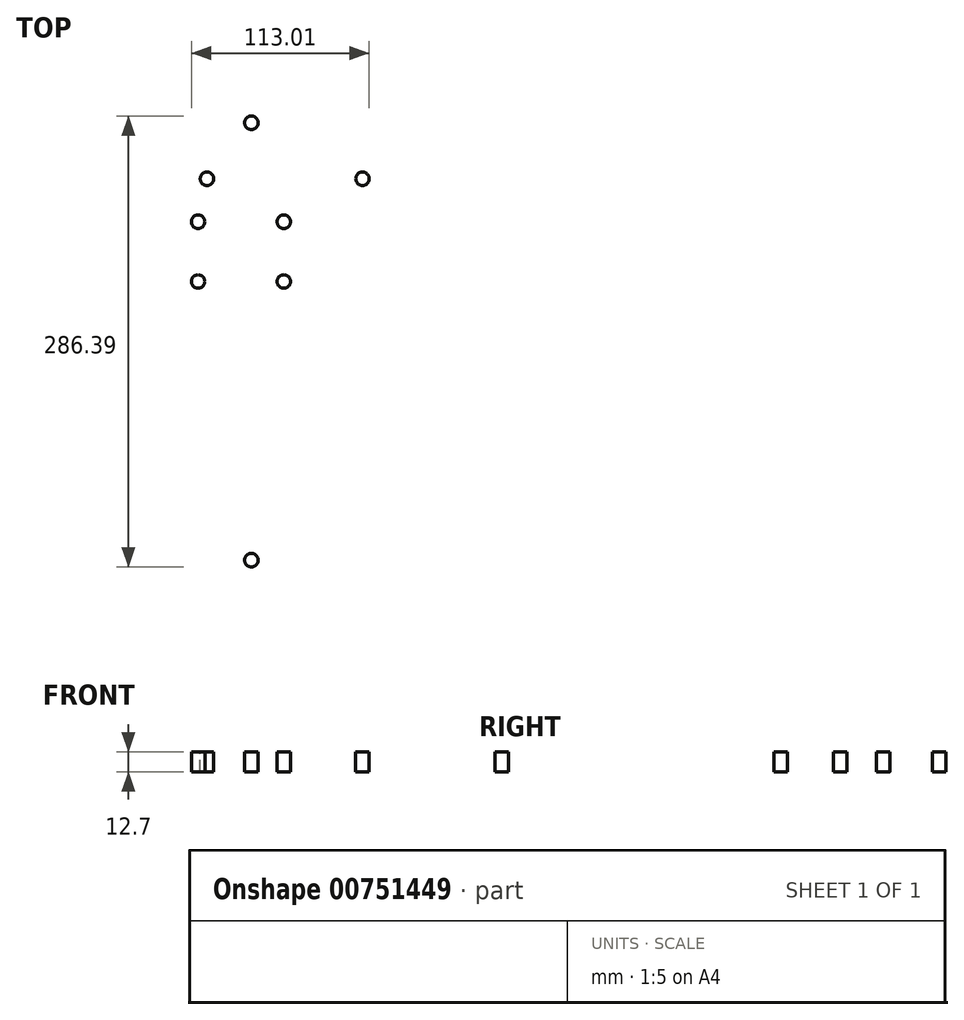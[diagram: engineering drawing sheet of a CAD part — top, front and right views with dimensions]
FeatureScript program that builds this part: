
annotation { "Feature Type Name" : "Feature", "Feature Type Description" : "" }
export const myFeature = defineFeature(function(context is Context, id is Id, definition is map)
    precondition{}
    {
        {
            var Q0;
            Q0=qCreatedBy(makeId("Top.planeOp"),FACE);
            var sketch = newSketch(context, id + "F0", { "sketchPlane" : qUnion([Q0])});
            skLineSegment(sketch, "E0.bottom", {"start": v(-266.7, 190.5) * mm, "end": v(266.7, 190.5) * mm});
            skLineSegment(sketch, "E0.top", {"start": v(-266.7, -190.5) * mm, "end": v(266.7, -190.5) * mm});
            skLineSegment(sketch, "E0.left", {"start": v(-266.7, 190.5) * mm, "end": v(-266.7, -190.5) * mm});
            skLineSegment(sketch, "E0.right", {"start": v(266.7, 190.5) * mm, "end": v(266.7, -190.5) * mm});
            skLineSegment(sketch, "E1", {"start": v(-266.7, 190.5) * mm, "end": v(266.7, -190.5) * mm, "construction": true});
            skLineSegment(sketch, "E2", {"start": v(266.7, 190.5) * mm, "end": v(-266.7, -190.5) * mm, "construction": true});
            skPoint(sketch, "E3", {"position": v(0, 0) * mm});
            skSolve(sketch);
        }
        {
            var Q0;
            Q0=makeQuery(id+"F0.imprint","IMPRINT",FACE,{"disambiguationData":[TD([[makeQuery(id+"F0.imprint","IMPRINT",EDGE,{"derivedFrom":sQuery(id+"F0.wireOp",EDGE,"E0.bottom")}),-1.0]])]});
            extrude(context, id + "F1", {"entities" : qUnion([Q0]), "depth" : 12.7 * mm, "offsetDistance" : 25.4 * mm});
        }
        {
            var Q0;
            Q0=makeQuery(id+"F1.opExtrude","CAP_FACE",FACE,{"disambiguationData":[OSD([sQuery(id+"F0.wireOp",EDGE,"E0.bottom"),sQuery(id+"F0.wireOp",EDGE,"E0.top"),sQuery(id+"F0.wireOp",EDGE,"E0.left"),sQuery(id+"F0.wireOp",EDGE,"E0.right")])],"isStart":false});
            var sketch = newSketch(context, id + "F2", { "sketchPlane" : qUnion([Q0])});
            skLineSegment(sketch, "E4.bottom", {"start": v(173.08, 152.4) * mm, "end": v(236.58, 152.4) * mm});
            skLineSegment(sketch, "E4.top", {"start": v(173.08, 63.5) * mm, "end": v(236.58, 63.5) * mm});
            skLineSegment(sketch, "E4.left", {"start": v(173.08, 152.4) * mm, "end": v(173.08, 63.5) * mm});
            skLineSegment(sketch, "E4.right", {"start": v(236.58, 152.4) * mm, "end": v(236.58, 63.5) * mm});
            skLineSegment(sketch, "E5.bottom", {"start": v(208.28, 28.07) * mm, "end": v(87.63, 28.07) * mm, "construction": true});
            skLineSegment(sketch, "E5.top", {"start": v(208.28, 92.08) * mm, "end": v(87.63, 92.07) * mm, "construction": true});
            skLineSegment(sketch, "E5.left", {"start": v(208.28, 28.07) * mm, "end": v(208.28, 92.08) * mm, "construction": true});
            skLineSegment(sketch, "E5.right", {"start": v(87.63, 28.07) * mm, "end": v(87.63, 92.07) * mm, "construction": true});
            skCircle(sketch, "E6", {"center": v(108.03, 79.06) * mm, "radius": 4.3 * mm});
            skCircle(sketch, "E7", {"center": v(108.03, 41.08) * mm, "radius": 4.3 * mm});
            skCircle(sketch, "E8", {"center": v(162.48, 41.08) * mm, "radius": 4.3 * mm});
            skCircle(sketch, "E9", {"center": v(162.48, 79.06) * mm, "radius": 4.3 * mm});
            skLineSegment(sketch, "E10.bottom", {"start": v(131, 125.41) * mm, "end": v(173.08, 125.41) * mm, "construction": true});
            skLineSegment(sketch, "E10.top", {"start": v(131, 87.31) * mm, "end": v(173.08, 87.31) * mm, "construction": true});
            skLineSegment(sketch, "E10.left", {"start": v(131, 125.41) * mm, "end": v(131, 87.31) * mm, "construction": true});
            skLineSegment(sketch, "E10.right", {"start": v(173.08, 125.41) * mm, "end": v(173.08, 87.31) * mm, "construction": true});
            skCircle(sketch, "E11", {"center": v(156.81, 106.36) * mm, "radius": 4.3 * mm});
            skPoint(sketch, "E12", {"position": v(173.08, 106.36) * mm});
            skLineSegment(sketch, "E13.bottom", {"start": v(40.4, 125.41) * mm, "end": v(101.52, 125.41) * mm, "construction": true});
            skLineSegment(sketch, "E13.top", {"start": v(40.4, 87.31) * mm, "end": v(101.52, 87.31) * mm, "construction": true});
            skLineSegment(sketch, "E13.left", {"start": v(40.4, 125.41) * mm, "end": v(40.4, 87.31) * mm, "construction": true});
            skLineSegment(sketch, "E13.right", {"start": v(101.52, 125.41) * mm, "end": v(101.52, 87.31) * mm, "construction": true});
            skCircle(sketch, "E14", {"center": v(58.04, 106.36) * mm, "radius": 4.29 * mm});
            skPoint(sketch, "E14.perimeterSnap0", {"position": v(40.4, 106.36) * mm});
            skLineSegment(sketch, "E15", {"start": v(0, 190.5) * mm, "end": v(0, -190.5) * mm, "construction": true});
            skLineSegment(sketch, "E16.MirrorCS", {"start": v(-40.4, 125.41) * mm, "end": v(-40.4, 87.31) * mm, "construction": true});
            skLineSegment(sketch, "E17.MirrorCS", {"start": v(-40.4, 87.31) * mm, "end": v(-101.52, 87.31) * mm, "construction": true});
            skLineSegment(sketch, "E18.MirrorCS", {"start": v(-101.52, 125.41) * mm, "end": v(-101.52, 87.31) * mm, "construction": true});
            skLineSegment(sketch, "E19.MirrorCS", {"start": v(-40.4, 125.41) * mm, "end": v(-101.52, 125.41) * mm, "construction": true});
            skCircle(sketch, "E20.MirrorC", {"center": v(-58.04, 106.36) * mm, "radius": 4.29 * mm});
            skPoint(sketch, "E21.MirrorP", {"position": v(-40.4, 106.36) * mm});
            skLineSegment(sketch, "E22.MirrorCS", {"start": v(-87.63, 28.07) * mm, "end": v(-87.63, 92.08) * mm, "construction": true});
            skLineSegment(sketch, "E23.MirrorCS", {"start": v(-208.28, 28.07) * mm, "end": v(-87.63, 28.07) * mm, "construction": true});
            skLineSegment(sketch, "E24.MirrorCS", {"start": v(-208.28, 92.08) * mm, "end": v(-87.63, 92.08) * mm, "construction": true});
            skLineSegment(sketch, "E25.MirrorCS", {"start": v(-131, 125.41) * mm, "end": v(-131, 87.31) * mm, "construction": true});
            skLineSegment(sketch, "E26.MirrorCS", {"start": v(-208.28, 28.07) * mm, "end": v(-208.28, 92.08) * mm, "construction": true});
            skLineSegment(sketch, "E27.MirrorCS", {"start": v(-173.08, 125.41) * mm, "end": v(-173.08, 87.31) * mm, "construction": true});
            skPoint(sketch, "E28.MirrorP", {"position": v(-173.08, 106.36) * mm});
            skLineSegment(sketch, "E29.MirrorCS", {"start": v(-173.08, 152.4) * mm, "end": v(-173.08, 63.5) * mm});
            skLineSegment(sketch, "E30.MirrorCS", {"start": v(-173.08, 152.4) * mm, "end": v(-236.58, 152.4) * mm});
            skLineSegment(sketch, "E31.MirrorCS", {"start": v(-236.58, 152.4) * mm, "end": v(-236.58, 63.5) * mm});
            skLineSegment(sketch, "E32.MirrorCS", {"start": v(-173.08, 63.5) * mm, "end": v(-236.58, 63.5) * mm});
            skLineSegment(sketch, "E33.MirrorCS", {"start": v(-131, 87.31) * mm, "end": v(-173.08, 87.31) * mm, "construction": true});
            skLineSegment(sketch, "E34.MirrorCS", {"start": v(-131, 125.41) * mm, "end": v(-173.08, 125.41) * mm, "construction": true});
            skCircle(sketch, "E35.MirrorC", {"center": v(-156.81, 106.36) * mm, "radius": 4.3 * mm});
            skCircle(sketch, "E36.MirrorC", {"center": v(-108.03, 79.06) * mm, "radius": 4.3 * mm});
            skCircle(sketch, "E37.MirrorC", {"center": v(-108.03, 41.08) * mm, "radius": 4.3 * mm});
            skCircle(sketch, "E38.MirrorC", {"center": v(-162.48, 41.08) * mm, "radius": 4.3 * mm});
            skCircle(sketch, "E39.MirrorC", {"center": v(-162.48, 79.06) * mm, "radius": 4.3 * mm});
            skCircle(sketch, "E40", {"center": v(128.63, 141.92) * mm, "radius": 4.29 * mm});
            skCircle(sketch, "E41.MirrorC", {"center": v(-128.63, 141.92) * mm, "radius": 4.29 * mm});
            skCircle(sketch, "E42", {"center": v(128.63, -135.9) * mm, "radius": 4.29 * mm, "construction": true});
            skCircle(sketch, "E43.MirrorC", {"center": v(-128.63, -135.89) * mm, "radius": 4.29 * mm});
            skLineSegment(sketch, "E44.bottom", {"start": v(-12.7, 97.47) * mm, "end": v(12.7, 97.47) * mm});
            skLineSegment(sketch, "E44.top", {"start": v(-12.7, 91.12) * mm, "end": v(12.7, 91.12) * mm});
            skLineSegment(sketch, "E44.left", {"start": v(-12.7, 97.47) * mm, "end": v(-12.7, 91.12) * mm});
            skLineSegment(sketch, "E44.right", {"start": v(12.7, 97.47) * mm, "end": v(12.7, 91.12) * mm});
            skPoint(sketch, "E45", {"position": v(0, 91.12) * mm});
            skLineSegment(sketch, "E46.bottom", {"start": v(-12.7, -8.76) * mm, "end": v(12.7, -8.76) * mm});
            skLineSegment(sketch, "E46.top", {"start": v(-12.7, -15.11) * mm, "end": v(12.7, -15.11) * mm});
            skLineSegment(sketch, "E46.left", {"start": v(-12.7, -8.76) * mm, "end": v(-12.7, -15.11) * mm});
            skLineSegment(sketch, "E46.right", {"start": v(12.7, -8.76) * mm, "end": v(12.7, -15.11) * mm});
            skPoint(sketch, "E47", {"position": v(0, -8.76) * mm});
            skLineSegment(sketch, "E48.bottom", {"start": v(-84.46, 53.47) * mm, "end": v(-78.1, 53.47) * mm});
            skLineSegment(sketch, "E48.top", {"start": v(-84.46, 28.07) * mm, "end": v(-78.1, 28.07) * mm});
            skLineSegment(sketch, "E48.left", {"start": v(-84.46, 53.47) * mm, "end": v(-84.46, 28.07) * mm});
            skLineSegment(sketch, "E48.right", {"start": v(-78.1, 53.47) * mm, "end": v(-78.1, 28.07) * mm});
            skLineSegment(sketch, "E49.MirrorCS", {"start": v(78.1, 53.47) * mm, "end": v(78.1, 28.07) * mm});
            skLineSegment(sketch, "E50.MirrorCS", {"start": v(84.46, 53.47) * mm, "end": v(78.1, 53.47) * mm});
            skLineSegment(sketch, "E51.MirrorCS", {"start": v(84.46, 53.47) * mm, "end": v(84.46, 28.07) * mm});
            skLineSegment(sketch, "E52.MirrorCS", {"start": v(84.46, 28.07) * mm, "end": v(78.1, 28.07) * mm});
            skLineSegment(sketch, "E53.bottom", {"start": v(90.53, -120.02) * mm, "end": v(166.73, -120.02) * mm, "construction": true});
            skLineSegment(sketch, "E53.top", {"start": v(90.53, -151.77) * mm, "end": v(166.73, -151.77) * mm, "construction": true});
            skLineSegment(sketch, "E53.left", {"start": v(90.53, -120.02) * mm, "end": v(90.53, -151.77) * mm, "construction": true});
            skLineSegment(sketch, "E53.right", {"start": v(166.73, -120.02) * mm, "end": v(166.73, -151.77) * mm, "construction": true});
            skLineSegment(sketch, "E54", {"start": v(166.73, -120.02) * mm, "end": v(90.53, -151.77) * mm, "construction": true});
            skLineSegment(sketch, "E55", {"start": v(90.53, -120.02) * mm, "end": v(166.73, -151.77) * mm, "construction": true});
            skLineSegment(sketch, "E56.MirrorCS", {"start": v(-166.73, -120.02) * mm, "end": v(-90.53, -151.77) * mm, "construction": true});
            skLineSegment(sketch, "E57.MirrorCS", {"start": v(-90.53, -120.01) * mm, "end": v(-166.73, -151.77) * mm, "construction": true});
            skLineSegment(sketch, "E58.MirrorCS", {"start": v(-90.53, -120.02) * mm, "end": v(-166.73, -120.02) * mm, "construction": true});
            skLineSegment(sketch, "E59.MirrorCS", {"start": v(-90.53, -151.77) * mm, "end": v(-166.73, -151.77) * mm, "construction": true});
            skLineSegment(sketch, "E60.MirrorCS", {"start": v(-166.73, -120.02) * mm, "end": v(-166.73, -151.77) * mm, "construction": true});
            skCircle(sketch, "E61.MirrorC", {"center": v(-128.63, -135.89) * mm, "radius": 4.29 * mm, "construction": true});
            skLineSegment(sketch, "E62.MirrorCS", {"start": v(-90.53, -120.02) * mm, "end": v(-90.53, -151.77) * mm, "construction": true});
            skSolve(sketch);
        }
        {
            var Q0;
            Q0=makeQuery(id+"F2.imprint","IMPRINT",FACE,{"disambiguationData":[TD([[makeQuery(id+"F2.imprint","IMPRINT",EDGE,{"derivedFrom":sQuery(id+"F2.wireOp",EDGE,"E4.bottom")}),-1.0]])]});
            var Q1;
            Q1=makeQuery(id+"F2.imprint","IMPRINT",FACE,{"disambiguationData":[TD([[makeQuery(id+"F2.imprint","IMPRINT",EDGE,{"derivedFrom":sQuery(id+"F2.wireOp",EDGE,"E6")}),1.0]])]});
            var Q2;
            Q2=makeQuery(id+"F2.imprint","IMPRINT",FACE,{"disambiguationData":[TD([[makeQuery(id+"F2.imprint","IMPRINT",EDGE,{"derivedFrom":sQuery(id+"F2.wireOp",EDGE,"E9")}),1.0]])]});
            var Q3;
            Q3=makeQuery(id+"F2.imprint","IMPRINT",FACE,{"disambiguationData":[TD([[makeQuery(id+"F2.imprint","IMPRINT",EDGE,{"derivedFrom":sQuery(id+"F2.wireOp",EDGE,"E8")}),1.0]])]});
            var Q4;
            Q4=makeQuery(id+"F2.imprint","IMPRINT",FACE,{"disambiguationData":[TD([[makeQuery(id+"F2.imprint","IMPRINT",EDGE,{"derivedFrom":sQuery(id+"F2.wireOp",EDGE,"E7")}),1.0]])]});
            var Q5;
            Q5=makeQuery(id+"F2.imprint","IMPRINT",FACE,{"disambiguationData":[TD([[makeQuery(id+"F2.imprint","IMPRINT",EDGE,{"derivedFrom":sQuery(id+"F2.wireOp",EDGE,"E14")}),1.0]])]});
            var Q6;
            Q6=makeQuery(id+"F2.imprint","IMPRINT",FACE,{"disambiguationData":[TD([[makeQuery(id+"F2.imprint","IMPRINT",EDGE,{"derivedFrom":sQuery(id+"F2.wireOp",EDGE,"E11")}),1.0]])]});
            var Q7;
            Q7=makeQuery(id+"F2.imprint","IMPRINT",FACE,{"disambiguationData":[TD([[makeQuery(id+"F2.imprint","IMPRINT",EDGE,{"derivedFrom":sQuery(id+"F2.wireOp",EDGE,"E29.MirrorCS")}),-1.0]])]});
            var Q8;
            Q8=makeQuery(id+"F2.imprint","IMPRINT",FACE,{"disambiguationData":[TD([[makeQuery(id+"F2.imprint","IMPRINT",EDGE,{"derivedFrom":sQuery(id+"F2.wireOp",EDGE,"E39.MirrorC")}),-1.0]])]});
            var Q9;
            Q9=makeQuery(id+"F2.imprint","IMPRINT",FACE,{"disambiguationData":[TD([[makeQuery(id+"F2.imprint","IMPRINT",EDGE,{"derivedFrom":sQuery(id+"F2.wireOp",EDGE,"E38.MirrorC")}),-1.0]])]});
            var Q10;
            Q10=makeQuery(id+"F2.imprint","IMPRINT",FACE,{"disambiguationData":[TD([[makeQuery(id+"F2.imprint","IMPRINT",EDGE,{"derivedFrom":sQuery(id+"F2.wireOp",EDGE,"E37.MirrorC")}),-1.0]])]});
            var Q11;
            Q11=makeQuery(id+"F2.imprint","IMPRINT",FACE,{"disambiguationData":[TD([[makeQuery(id+"F2.imprint","IMPRINT",EDGE,{"derivedFrom":sQuery(id+"F2.wireOp",EDGE,"E36.MirrorC")}),-1.0]])]});
            var Q12;
            Q12=makeQuery(id+"F2.imprint","IMPRINT",FACE,{"disambiguationData":[TD([[makeQuery(id+"F2.imprint","IMPRINT",EDGE,{"derivedFrom":sQuery(id+"F2.wireOp",EDGE,"E35.MirrorC")}),-1.0]])]});
            var Q13;
            Q13=makeQuery(id+"F2.imprint","IMPRINT",FACE,{"disambiguationData":[TD([[makeQuery(id+"F2.imprint","IMPRINT",EDGE,{"derivedFrom":sQuery(id+"F2.wireOp",EDGE,"E20.MirrorC")}),-1.0]])]});
            var Q14;
            Q14=makeQuery(id+"F2.imprint","IMPRINT",FACE,{"disambiguationData":[TD([[makeQuery(id+"F2.imprint","IMPRINT",EDGE,{"derivedFrom":sQuery(id+"F2.wireOp",EDGE,"E40")}),1.0]])]});
            var Q15;
            Q15=makeQuery(id+"F2.imprint","IMPRINT",FACE,{"disambiguationData":[TD([[makeQuery(id+"F2.imprint","IMPRINT",EDGE,{"derivedFrom":sQuery(id+"F2.wireOp",EDGE,"E41.MirrorC")}),-1.0]])]});
            var Q16;
            Q16=makeQuery(id+"F2.imprint","IMPRINT",FACE,{"disambiguationData":[TD([[makeQuery(id+"F2.imprint","IMPRINT",EDGE,{"derivedFrom":sQuery(id+"F2.wireOp",EDGE,"E42")}),1.0]])]});
            var Q17;
            Q17=makeQuery(id+"F2.imprint","IMPRINT",FACE,{"disambiguationData":[TD([[makeQuery(id+"F2.imprint","IMPRINT",EDGE,{"derivedFrom":sQuery(id+"F2.wireOp",EDGE,"E43.MirrorC")}),-1.0]])]});
            var Q18;
            Q18=makeQuery(id+"F2.imprint","IMPRINT",FACE,{"disambiguationData":[TD([[makeQuery(id+"F2.imprint","IMPRINT",EDGE,{"derivedFrom":sQuery(id+"F2.wireOp",EDGE,"E48.bottom")}),-1.0]])]});
            var Q19;
            Q19=makeQuery(id+"F2.imprint","IMPRINT",FACE,{"disambiguationData":[TD([[makeQuery(id+"F2.imprint","IMPRINT",EDGE,{"derivedFrom":sQuery(id+"F2.wireOp",EDGE,"E44.bottom")}),-1.0]])]});
            var Q20;
            Q20=makeQuery(id+"F2.imprint","IMPRINT",FACE,{"disambiguationData":[TD([[makeQuery(id+"F2.imprint","IMPRINT",EDGE,{"derivedFrom":sQuery(id+"F2.wireOp",EDGE,"E49.MirrorCS")}),1.0]])]});
            var Q21;
            Q21=makeQuery(id+"F2.imprint","IMPRINT",FACE,{"disambiguationData":[TD([[makeQuery(id+"F2.imprint","IMPRINT",EDGE,{"derivedFrom":sQuery(id+"F2.wireOp",EDGE,"E46.bottom")}),-1.0]])]});
            extrude(context, id + "F3", {"entities" : qUnion([Q0, Q1, Q2, Q3, Q4, Q5, Q6, Q7, Q8, Q9, Q10, Q11, Q12, Q13, Q14, Q15, Q16, Q17, Q18, Q19, Q20, Q21]), "operationType" : NewBodyOperationType.REMOVE, "endBound" : BoundingType.THROUGH_ALL, "oppositeDirection" : true, "depth" : 25.4 * mm, "offsetDistance" : 25.4 * mm});
        }
        {
            var Q0;
            Q0=makeQuery(id+"F2.imprint","IMPRINT",FACE,{"disambiguationData":[TD([[makeQuery(id+"F2.imprint","IMPRINT",EDGE,{"derivedFrom":sQuery(id+"F2.wireOp",EDGE,"E4.bottom")}),1.0]])]});
            var sketch = newSketch(context, id + "F4", { "sketchPlane" : qUnion([Q0])});
            skLineSegment(sketch, "E63.bottom", {"start": v(-75, 87.31) * mm, "end": v(75, 87.31) * mm});
            skLineSegment(sketch, "E63.top", {"start": v(-75, -6.69) * mm, "end": v(75, -6.69) * mm});
            skLineSegment(sketch, "E63.left", {"start": v(-75, 87.31) * mm, "end": v(-75, -6.69) * mm});
            skLineSegment(sketch, "E63.right", {"start": v(75, 87.31) * mm, "end": v(75, -6.69) * mm});
            skPoint(sketch, "E64", {"position": v(0, 87.31) * mm});
            skLineSegment(sketch, "E65.bottom", {"start": v(125.41, -10.03) * mm, "end": v(188.91, -10.03) * mm});
            skLineSegment(sketch, "E65.top", {"start": v(125.41, -104.01) * mm, "end": v(188.91, -104.01) * mm});
            skLineSegment(sketch, "E65.left", {"start": v(125.41, -10.03) * mm, "end": v(125.41, -104.01) * mm});
            skLineSegment(sketch, "E65.right", {"start": v(188.91, -10.03) * mm, "end": v(188.91, -104.01) * mm});
            skLineSegment(sketch, "E66.bottom", {"start": v(-80.96, -31.47) * mm, "end": v(80.96, -31.47) * mm});
            skLineSegment(sketch, "E66.top", {"start": v(-80.96, -145.77) * mm, "end": v(80.96, -145.77) * mm});
            skLineSegment(sketch, "E66.left", {"start": v(-80.96, -31.47) * mm, "end": v(-80.96, -145.77) * mm});
            skLineSegment(sketch, "E66.right", {"start": v(80.96, -31.47) * mm, "end": v(80.96, -145.77) * mm});
            skPoint(sketch, "E67", {"position": v(157.16, -10.03) * mm});
            skPoint(sketch, "E68", {"position": v(0, -31.47) * mm});
            skLineSegment(sketch, "E69.bottom", {"start": v(-266.7, -160.38) * mm, "end": v(266.7, -160.38) * mm, "construction": true});
            skLineSegment(sketch, "E69.top", {"start": v(-266.7, -190.5) * mm, "end": v(266.7, -190.5) * mm, "construction": true});
            skLineSegment(sketch, "E69.left", {"start": v(-266.7, -160.38) * mm, "end": v(-266.7, -190.5) * mm, "construction": true});
            skLineSegment(sketch, "E69.right", {"start": v(266.7, -160.38) * mm, "end": v(266.7, -190.5) * mm, "construction": true});
            skLineSegment(sketch, "E70.bottom", {"start": v(-266.7, -190.5) * mm, "end": v(-236.58, -190.5) * mm, "construction": true});
            skLineSegment(sketch, "E70.top", {"start": v(-266.7, 190.5) * mm, "end": v(-236.58, 190.5) * mm, "construction": true});
            skLineSegment(sketch, "E70.left", {"start": v(-266.7, -190.5) * mm, "end": v(-266.7, 190.5) * mm, "construction": true});
            skLineSegment(sketch, "E70.right", {"start": v(-236.58, -190.5) * mm, "end": v(-236.58, 190.5) * mm, "construction": true});
            skLineSegment(sketch, "E71.bottom", {"start": v(266.7, -190.5) * mm, "end": v(236.58, -190.5) * mm, "construction": true});
            skLineSegment(sketch, "E71.top", {"start": v(266.7, 190.5) * mm, "end": v(236.58, 190.5) * mm, "construction": true});
            skLineSegment(sketch, "E71.left", {"start": v(266.7, -190.5) * mm, "end": v(266.7, 190.5) * mm, "construction": true});
            skLineSegment(sketch, "E71.right", {"start": v(236.58, -190.5) * mm, "end": v(236.58, 190.5) * mm, "construction": true});
            skLineSegment(sketch, "E72.bottom", {"start": v(-266.7, 190.5) * mm, "end": v(266.7, 190.5) * mm, "construction": true});
            skLineSegment(sketch, "E72.top", {"start": v(-266.7, 160.38) * mm, "end": v(266.7, 160.38) * mm, "construction": true});
            skLineSegment(sketch, "E72.left", {"start": v(-266.7, 190.5) * mm, "end": v(-266.7, 160.38) * mm, "construction": true});
            skLineSegment(sketch, "E72.right", {"start": v(266.7, 190.5) * mm, "end": v(266.7, 160.38) * mm, "construction": true});
            skPoint(sketch, "E73", {"position": v(80.96, -88.62) * mm});
            skPoint(sketch, "E74", {"position": v(125.41, -57.02) * mm});
            skLineSegment(sketch, "E75.bottom", {"start": v(-223.88, -22.73) * mm, "end": v(-93.66, -22.73) * mm, "construction": true});
            skLineSegment(sketch, "E75.top", {"start": v(-223.88, -107.32) * mm, "end": v(-93.66, -107.32) * mm, "construction": true});
            skLineSegment(sketch, "E75.left", {"start": v(-223.88, -22.73) * mm, "end": v(-223.88, -107.32) * mm, "construction": true});
            skLineSegment(sketch, "E75.right", {"start": v(-93.66, -22.73) * mm, "end": v(-93.66, -107.31) * mm, "construction": true});
            skLineSegment(sketch, "E76.bottom", {"start": v(87.7, 15.37) * mm, "end": v(113.1, 15.37) * mm});
            skLineSegment(sketch, "E76.top", {"start": v(87.7, -16.38) * mm, "end": v(113.1, -16.38) * mm});
            skLineSegment(sketch, "E76.left", {"start": v(87.7, 15.37) * mm, "end": v(87.7, -16.38) * mm});
            skLineSegment(sketch, "E76.right", {"start": v(113.1, 15.37) * mm, "end": v(113.1, -16.38) * mm});
            skLineSegment(sketch, "E77.bottom", {"start": v(-119.45, 15.37) * mm, "end": v(-87.7, 15.37) * mm});
            skLineSegment(sketch, "E77.top", {"start": v(-119.45, -10.03) * mm, "end": v(-87.7, -10.03) * mm});
            skLineSegment(sketch, "E77.left", {"start": v(-119.45, 15.37) * mm, "end": v(-119.45, -10.03) * mm});
            skLineSegment(sketch, "E77.right", {"start": v(-87.7, 15.37) * mm, "end": v(-87.7, -10.03) * mm});
            skLineSegment(sketch, "E78.bottom", {"start": v(207.96, -72.26) * mm, "end": v(233.36, -72.26) * mm});
            skLineSegment(sketch, "E78.top", {"start": v(207.96, -104.01) * mm, "end": v(233.36, -104.01) * mm});
            skLineSegment(sketch, "E78.left", {"start": v(207.96, -72.26) * mm, "end": v(207.96, -104.01) * mm});
            skLineSegment(sketch, "E78.right", {"start": v(233.36, -72.26) * mm, "end": v(233.36, -104.01) * mm});
            skLineSegment(sketch, "E79.bottom", {"start": v(-33.34, -63.22) * mm, "end": v(36.66, -63.22) * mm});
            skLineSegment(sketch, "E79.top", {"start": v(-33.34, -118.22) * mm, "end": v(36.66, -118.22) * mm});
            skLineSegment(sketch, "E79.left", {"start": v(-33.34, -63.22) * mm, "end": v(-33.34, -118.22) * mm});
            skLineSegment(sketch, "E79.right", {"start": v(36.66, -63.22) * mm, "end": v(36.66, -118.22) * mm});
            skLineSegment(sketch, "E80", {"start": v(-119.45, -10.03) * mm, "end": v(-87.7, 15.37) * mm, "construction": true});
            skLineSegment(sketch, "E81", {"start": v(-119.45, 15.37) * mm, "end": v(-87.7, -10.03) * mm, "construction": true});
            skPoint(sketch, "E82", {"position": v(-103.57, 2.67) * mm});
            skPoint(sketch, "E83", {"position": v(0, -90.72) * mm});
            skPoint(sketch, "E83.positionSnap0", {"position": v(-33.34, -90.72) * mm});
            skPoint(sketch, "E84", {"position": v(157.16, -57.02) * mm});
            skPoint(sketch, "E84.positionSnap0", {"position": v(188.91, -57.02) * mm});
            skPoint(sketch, "E85", {"position": v(220.66, -88.14) * mm});
            skPoint(sketch, "E85.positionSnap0", {"position": v(220.66, -72.26) * mm});
            skPoint(sketch, "E85.positionSnap1", {"position": v(207.96, -88.14) * mm});
            skPoint(sketch, "E86", {"position": v(100.4, -0.5) * mm});
            skPoint(sketch, "E86.positionSnap0", {"position": v(87.7, -0.5) * mm});
            skPoint(sketch, "E86.positionSnap1", {"position": v(100.4, 15.37) * mm});
            skPoint(sketch, "E87", {"position": v(0, 40.31) * mm});
            skPoint(sketch, "E87.positionSnap0", {"position": v(-75, 40.31) * mm});
            skCircle(sketch, "E88", {"center": v(-133.35, 173.99) * mm, "radius": 4.29 * mm});
            skCircle(sketch, "E89", {"center": v(0, 173.99) * mm, "radius": 4.29 * mm});
            skCircle(sketch, "E90", {"center": v(133.35, 173.99) * mm, "radius": 4.29 * mm});
            skCircle(sketch, "E91", {"center": v(250.2, 0) * mm, "radius": 4.29 * mm});
            skLineSegment(sketch, "E92", {"start": v(0, 190.5) * mm, "end": v(0, -190.5) * mm, "construction": true});
            skLineSegment(sketch, "E93", {"start": v(266.7, 0) * mm, "end": v(-266.7, 0) * mm, "construction": true});
            skCircle(sketch, "E94.MirrorC", {"center": v(-250.2, 0) * mm, "radius": 4.29 * mm});
            skCircle(sketch, "E95.MirrorC", {"center": v(0, -173.99) * mm, "radius": 4.29 * mm});
            skCircle(sketch, "E96.MirrorC", {"center": v(133.35, -173.99) * mm, "radius": 4.29 * mm});
            skCircle(sketch, "E97.MirrorC", {"center": v(-133.35, -173.99) * mm, "radius": 4.29 * mm});
            skSolve(sketch);
        }
        {
            var Q0;
            Q0=makeQuery(id+"F2.imprint","IMPRINT",FACE,{"disambiguationData":[TD([[makeQuery(id+"F2.imprint","IMPRINT",EDGE,{"derivedFrom":sQuery(id+"F2.wireOp",EDGE,"E4.bottom")}),1.0]])]});
            var sketch = newSketch(context, id + "F5", { "sketchPlane" : qUnion([Q0])});
            skLineSegment(sketch, "E98.bottom", {"start": v(-12.7, -21.31) * mm, "end": v(12.7, -21.31) * mm});
            skLineSegment(sketch, "E98.top", {"start": v(-12.7, -27.66) * mm, "end": v(12.7, -27.66) * mm});
            skLineSegment(sketch, "E98.left", {"start": v(-12.7, -21.31) * mm, "end": v(-12.7, -27.66) * mm});
            skLineSegment(sketch, "E98.right", {"start": v(12.7, -21.31) * mm, "end": v(12.7, -27.66) * mm});
            skLineSegment(sketch, "E99.bottom", {"start": v(84.77, -75.92) * mm, "end": v(91.12, -75.92) * mm});
            skLineSegment(sketch, "E99.top", {"start": v(84.77, -101.32) * mm, "end": v(91.12, -101.32) * mm});
            skLineSegment(sketch, "E99.left", {"start": v(84.77, -75.92) * mm, "end": v(84.77, -101.32) * mm});
            skLineSegment(sketch, "E99.right", {"start": v(91.12, -75.92) * mm, "end": v(91.12, -101.32) * mm});
            skLineSegment(sketch, "E100.bottom", {"start": v(-12.7, -149.58) * mm, "end": v(12.7, -149.58) * mm});
            skLineSegment(sketch, "E100.top", {"start": v(-12.7, -155.93) * mm, "end": v(12.7, -155.93) * mm});
            skLineSegment(sketch, "E100.left", {"start": v(-12.7, -149.58) * mm, "end": v(-12.7, -155.93) * mm});
            skLineSegment(sketch, "E100.right", {"start": v(12.7, -149.58) * mm, "end": v(12.7, -155.93) * mm});
            skPoint(sketch, "E101", {"position": v(0, -27.66) * mm});
            skPoint(sketch, "E102", {"position": v(84.77, -88.62) * mm});
            skPoint(sketch, "E103", {"position": v(0, -149.58) * mm});
            skLineSegment(sketch, "E104.MirrorCS", {"start": v(-84.77, -75.92) * mm, "end": v(-84.77, -101.32) * mm});
            skLineSegment(sketch, "E105.MirrorCS", {"start": v(-84.77, -101.32) * mm, "end": v(-91.12, -101.32) * mm});
            skLineSegment(sketch, "E106.MirrorCS", {"start": v(-91.12, -75.92) * mm, "end": v(-91.12, -101.32) * mm});
            skLineSegment(sketch, "E107.MirrorCS", {"start": v(-84.77, -75.92) * mm, "end": v(-91.12, -75.92) * mm});
            skCircle(sketch, "E108", {"center": v(-103.57, 20.45) * mm, "radius": 3.18 * mm});
            skCircle(sketch, "E109", {"center": v(-103.57, -15.11) * mm, "radius": 3.18 * mm});
            skCircle(sketch, "E110", {"center": v(220.66, -67.18) * mm, "radius": 3.18 * mm});
            skCircle(sketch, "E111", {"center": v(220.66, -109.1) * mm, "radius": 3.18 * mm});
            skCircle(sketch, "E112", {"center": v(100.4, 20.45) * mm, "radius": 3.18 * mm});
            skCircle(sketch, "E113", {"center": v(100.4, -21.46) * mm, "radius": 3.18 * mm});
            skLineSegment(sketch, "E114.bottom", {"start": v(115.25, -44.32) * mm, "end": v(121.6, -44.32) * mm});
            skLineSegment(sketch, "E114.top", {"start": v(115.25, -69.72) * mm, "end": v(121.6, -69.72) * mm});
            skLineSegment(sketch, "E114.left", {"start": v(115.25, -44.32) * mm, "end": v(115.25, -69.72) * mm});
            skLineSegment(sketch, "E114.right", {"start": v(121.6, -44.32) * mm, "end": v(121.6, -69.72) * mm});
            skPoint(sketch, "E115", {"position": v(115.25, -57.02) * mm});
            skLineSegment(sketch, "E116.bottom", {"start": v(192.72, -44.32) * mm, "end": v(199.07, -44.32) * mm});
            skLineSegment(sketch, "E116.top", {"start": v(192.72, -69.72) * mm, "end": v(199.07, -69.72) * mm});
            skLineSegment(sketch, "E116.left", {"start": v(192.72, -44.32) * mm, "end": v(192.72, -69.72) * mm});
            skLineSegment(sketch, "E116.right", {"start": v(199.07, -44.32) * mm, "end": v(199.07, -69.72) * mm});
            skPoint(sketch, "E117", {"position": v(192.72, -57.02) * mm});
            skSolve(sketch);
        }
        {
            var Q0;
            Q0=makeQuery(id+"F5.imprint","IMPRINT",FACE,{"disambiguationData":[TD([[makeQuery(id+"F5.imprint","IMPRINT",EDGE,{"derivedFrom":sQuery(id+"F5.wireOp",EDGE,"E98.bottom")}),-1.0]])]});
            var Q1;
            Q1=makeQuery(id+"F5.imprint","IMPRINT",FACE,{"disambiguationData":[TD([[makeQuery(id+"F5.imprint","IMPRINT",EDGE,{"derivedFrom":sQuery(id+"F5.wireOp",EDGE,"E104.MirrorCS")}),-1.0]])]});
            var Q2;
            Q2=makeQuery(id+"F5.imprint","IMPRINT",FACE,{"disambiguationData":[TD([[makeQuery(id+"F5.imprint","IMPRINT",EDGE,{"derivedFrom":sQuery(id+"F5.wireOp",EDGE,"E100.bottom")}),-1.0]])]});
            var Q3;
            Q3=makeQuery(id+"F5.imprint","IMPRINT",FACE,{"disambiguationData":[TD([[makeQuery(id+"F5.imprint","IMPRINT",EDGE,{"derivedFrom":sQuery(id+"F5.wireOp",EDGE,"E99.bottom")}),-1.0]])]});
            var Q4;
            Q4=makeQuery(id+"F5.imprint","IMPRINT",FACE,{"disambiguationData":[TD([[makeQuery(id+"F5.imprint","IMPRINT",EDGE,{"derivedFrom":sQuery(id+"F5.wireOp",EDGE,"E111")}),1.0]])]});
            var Q5;
            Q5=makeQuery(id+"F5.imprint","IMPRINT",FACE,{"disambiguationData":[TD([[makeQuery(id+"F5.imprint","IMPRINT",EDGE,{"derivedFrom":sQuery(id+"F5.wireOp",EDGE,"E110")}),1.0]])]});
            var Q6;
            Q6=makeQuery(id+"F5.imprint","IMPRINT",FACE,{"disambiguationData":[TD([[makeQuery(id+"F5.imprint","IMPRINT",EDGE,{"derivedFrom":sQuery(id+"F5.wireOp",EDGE,"E112")}),1.0]])]});
            var Q7;
            Q7=makeQuery(id+"F5.imprint","IMPRINT",FACE,{"disambiguationData":[TD([[makeQuery(id+"F5.imprint","IMPRINT",EDGE,{"derivedFrom":sQuery(id+"F5.wireOp",EDGE,"E113")}),1.0]])]});
            var Q8;
            Q8=makeQuery(id+"F5.imprint","IMPRINT",FACE,{"disambiguationData":[TD([[makeQuery(id+"F5.imprint","IMPRINT",EDGE,{"derivedFrom":sQuery(id+"F5.wireOp",EDGE,"E109")}),1.0]])]});
            var Q9;
            Q9=makeQuery(id+"F5.imprint","IMPRINT",FACE,{"disambiguationData":[TD([[makeQuery(id+"F5.imprint","IMPRINT",EDGE,{"derivedFrom":sQuery(id+"F5.wireOp",EDGE,"E108")}),1.0]])]});
            var Q10;
            Q10=makeQuery(id+"F5.imprint","IMPRINT",FACE,{"disambiguationData":[TD([[makeQuery(id+"F5.imprint","IMPRINT",EDGE,{"derivedFrom":sQuery(id+"F5.wireOp",EDGE,"E114.bottom")}),-1.0]])]});
            var Q11;
            Q11=makeQuery(id+"F5.imprint","IMPRINT",FACE,{"disambiguationData":[TD([[makeQuery(id+"F5.imprint","IMPRINT",EDGE,{"derivedFrom":sQuery(id+"F5.wireOp",EDGE,"E116.bottom")}),-1.0]])]});
            var Q12;
            Q12=makeQuery(id+"F4.imprint","IMPRINT",FACE,{"disambiguationData":[TD([[makeQuery(id+"F4.imprint","IMPRINT",EDGE,{"derivedFrom":sQuery(id+"F4.wireOp",EDGE,"E90")}),1.0]])]});
            var Q13;
            Q13=makeQuery(id+"F4.imprint","IMPRINT",FACE,{"disambiguationData":[TD([[makeQuery(id+"F4.imprint","IMPRINT",EDGE,{"derivedFrom":sQuery(id+"F4.wireOp",EDGE,"E89")}),1.0]])]});
            var Q14;
            Q14=makeQuery(id+"F4.imprint","IMPRINT",FACE,{"disambiguationData":[TD([[makeQuery(id+"F4.imprint","IMPRINT",EDGE,{"derivedFrom":sQuery(id+"F4.wireOp",EDGE,"E88")}),1.0]])]});
            var Q15;
            Q15=makeQuery(id+"F4.imprint","IMPRINT",FACE,{"disambiguationData":[TD([[makeQuery(id+"F4.imprint","IMPRINT",EDGE,{"derivedFrom":sQuery(id+"F4.wireOp",EDGE,"E97.MirrorC")}),-1.0]])]});
            var Q16;
            Q16=makeQuery(id+"F4.imprint","IMPRINT",FACE,{"disambiguationData":[TD([[makeQuery(id+"F4.imprint","IMPRINT",EDGE,{"derivedFrom":sQuery(id+"F4.wireOp",EDGE,"E95.MirrorC")}),-1.0]])]});
            var Q17;
            Q17=makeQuery(id+"F4.imprint","IMPRINT",FACE,{"disambiguationData":[TD([[makeQuery(id+"F4.imprint","IMPRINT",EDGE,{"derivedFrom":sQuery(id+"F4.wireOp",EDGE,"E96.MirrorC")}),-1.0]])]});
            var Q18;
            Q18=makeQuery(id+"F4.imprint","IMPRINT",FACE,{"disambiguationData":[TD([[makeQuery(id+"F4.imprint","IMPRINT",EDGE,{"derivedFrom":sQuery(id+"F4.wireOp",EDGE,"E91")}),1.0]])]});
            var Q19;
            Q19=makeQuery(id+"F4.imprint","IMPRINT",FACE,{"disambiguationData":[TD([[makeQuery(id+"F4.imprint","IMPRINT",EDGE,{"derivedFrom":sQuery(id+"F4.wireOp",EDGE,"E94.MirrorC")}),-1.0]])]});
            extrude(context, id + "F6", {"entities" : qUnion([Q0, Q1, Q2, Q3, Q4, Q5, Q6, Q7, Q8, Q9, Q10, Q11, Q12, Q13, Q14, Q15, Q16, Q17, Q18, Q19]), "operationType" : NewBodyOperationType.REMOVE, "endBound" : BoundingType.THROUGH_ALL, "oppositeDirection" : true, "depth" : 25.4 * mm, "offsetDistance" : 25.4 * mm});
        }
    });
